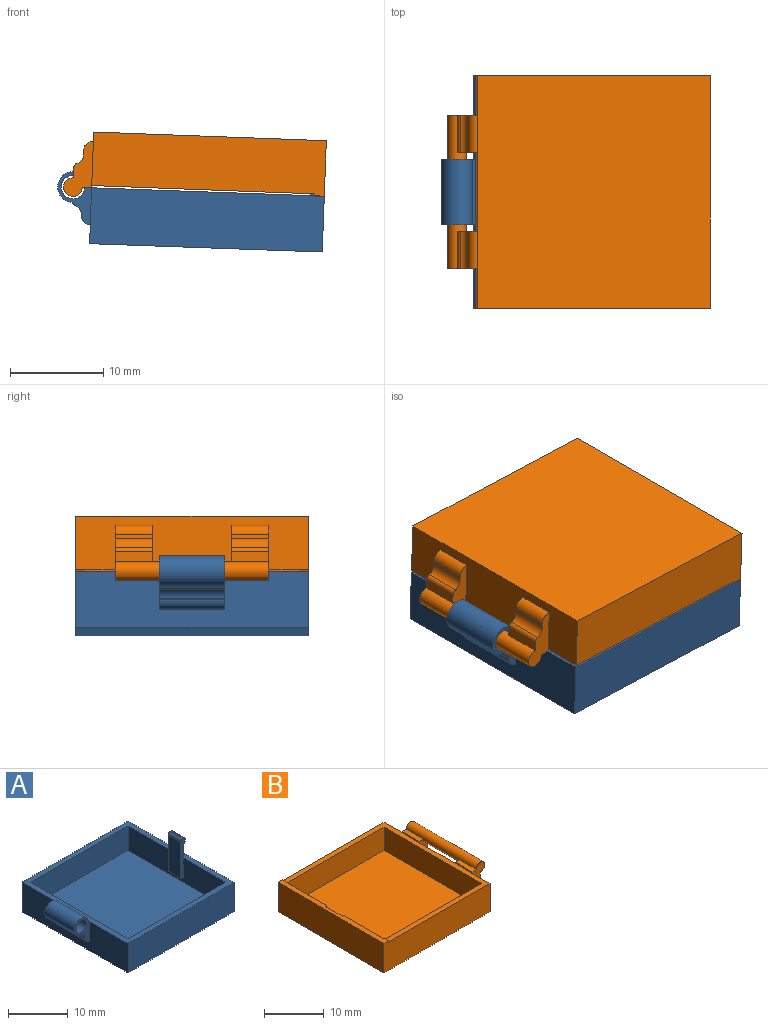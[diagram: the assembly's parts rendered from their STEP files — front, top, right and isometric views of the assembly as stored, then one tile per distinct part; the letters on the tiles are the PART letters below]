
ASSEMBLY  parts=2 mates=1
PART A: 30 faces, bbox 28.7x25x9.9 mm
  f0: plane 25x6mm, normal (-1,0,0), area 122mm2, adj f1,f2,f8,f9,f11,f12,f14
  f1: plane 25x6mm, normal (0,1,0), area 150mm2, adj f0,f7,f8,f9
  f2: plane 25x6mm, normal (0,-1,0), area 150mm2, adj f0,f7,f8,f9
  f3: plane 23x5mm, normal (0,-1,0), area 115mm2, adj f4,f6,f8,f10
  f4: plane 23x5mm, normal (-1,0,0), area 103mm2, adj f3,f5,f8,f10,f19,f20,f21
  f5: plane 23x5mm, normal (0,1,0), area 115mm2, adj f4,f6,f8,f10
  f6: plane 23x5mm, normal (1,0,0), area 115mm2, adj f3,f5,f8,f10
  f7: plane 25x6mm, normal (1,0,0), area 150mm2, adj f1,f2,f8,f9
  f8: plane 25.35x25mm, normal (0,0,1), area 98.4mm2, adj f0,f1,f2,f3,f4,f5,f6,f7
  f9: plane 25x25mm, normal (0,0,-1), area 625mm2, adj f0,f1,f2,f7
  f10: plane 23x23mm, normal (0,0,1), area 529mm2, adj f3,f4,f5,f6
  f11: plane 5.65x3.65mm, normal (0,1,0), area 7.4mm2, adj f0,f8,f13,f14,f15,f16,f17,f18
  f12: plane 5.65x3.65mm, normal (0,-1,0), area 7.4mm2, adj f0,f8,f13,f14,f15,f16,f17,f18
  f13: plane 7x0.09mm, normal (-1,0,0), area 0.6mm2, adj f11,f12,f14,f16
  f14: cylinder r=1mm len=7mm, axis (0,1,0), area 11mm2, adj f0,f11,f12,f13
  f15: cylinder r=0.5mm len=7mm, axis (0,1,0), area 3.2mm2, adj f11,f12,f16,f18
  f16: cylinder r=1mm len=7mm, axis (0,1,0), area 8.6mm2, adj f11,f12,f13,f15
  f17: cylinder r=1.25mm len=7mm, axis (0,-1,0), area 55mm2, adj f11,f12
  f18: cylinder r=1.65mm len=7mm, axis (0,-1,0), area 54.6mm2, adj f8,f11,f12,f15
  f19: plane 7.9x1mm, normal (0,1,0), area 4.4mm2, adj f4,f20,f22,f23,f24,f25,f26,f27
  f20: plane 3x0.5mm, normal (0,0,-1), area 1.5mm2, adj f4,f19,f21,f23
  f21: plane 7.9x1mm, normal (0,-1,0), area 4.4mm2, adj f4,f20,f22,f23,f24,f25,f26,f27
  f22: plane 3x0.25mm, normal (0,0,1), area 0.8mm2, adj f19,f21,f27,f29
  f23: plane 7.4x3mm, normal (-1,0,0), area 22.2mm2, adj f19,f20,f21,f29
  f24: plane 3x2.9mm, normal (1,0,0), area 8.7mm2, adj f8,f19,f21,f25
  f25: plane 3x0.25mm, normal (0,0,-1), area 0.8mm2, adj f19,f21,f24,f28
  f26: plane 3x0.5mm, normal (1,0,0), area 1.5mm2, adj f19,f21,f27,f28
  f27: cylinder r=0.25mm len=3mm, axis (0,1,0), area 1.2mm2, adj f19,f21,f22,f26
  f28: cylinder r=0.25mm len=3mm, axis (0,1,0), area 1.2mm2, adj f19,f21,f25,f26
  f29: cylinder r=0.5mm len=3mm, axis (0,-1,0), area 2.4mm2, adj f19,f21,f22,f23
PART B: 40 faces, bbox 28x25x7 mm
  f0: plane 4x1mm, normal (0,0,1), area 4mm2, adj f16,f17,f27,f35
  f1: plane 4x1mm, normal (0,0,1), area 4mm2, adj f13,f14,f27,f36
  f2: plane 25x6mm, normal (0,1,0), area 144mm2, adj f4,f8,f10,f11,f37,f39
  f3: plane 25x6mm, normal (0,-1,0), area 144mm2, adj f4,f8,f10,f11,f38,f39
  f4: plane 25x5.75mm, normal (1,0,0), area 105.8mm2, adj f2,f3,f11,f13,f14,f16,f17,f21
  f5: plane 23x4.75mm, normal (-1,0,0), area 109.2mm2, adj f6,f7,f12,f39
  f6: plane 23x5mm, normal (0,1,0), area 109.3mm2, adj f5,f8,f9,f12,f38,f39
  f7: plane 23x5mm, normal (0,-1,0), area 109.3mm2, adj f5,f8,f9,f12,f37,f39
  f8: plane 25x1.1mm, normal (0,0,1), area 23.8mm2, adj f2,f3,f6,f7,f9,f10,f31,f33
  f9: plane 23x5mm, normal (1,0,0), area 99mm2, adj f6,f7,f8,f12,f29,f30,f31,f33
  f10: plane 25x6mm, normal (-1,0,0), area 150mm2, adj f2,f3,f8,f11
  f11: plane 25x25mm, normal (0,0,-1), area 625mm2, adj f2,f3,f4,f10
  f12: plane 23x23mm, normal (0,0,1), area 529mm2, adj f5,f6,f7,f9
  f13: plane 6x3mm, normal (0,-1,0), area 9.8mm2, adj f1,f4,f15,f19,f22,f24,f26,f27
  f14: plane 5x2mm, normal (0,1,0), area 6.7mm2, adj f1,f4,f15,f19,f22,f24,f26,f27
  f15: plane 4x1.09mm, normal (1,0,0), area 4.3mm2, adj f13,f14,f26,f27
  f16: plane 5x2mm, normal (0,-1,0), area 6.7mm2, adj f0,f4,f18,f20,f21,f23,f25,f27
  f17: plane 6x3mm, normal (0,1,0), area 9.8mm2, adj f0,f4,f18,f20,f21,f23,f25,f27
  f18: plane 4x1.09mm, normal (1,0,0), area 4.3mm2, adj f16,f17,f25,f27
  f19: plane 4x0.5mm, normal (1,0,0), area 2mm2, adj f13,f14,f22,f24
  f20: plane 4x0.5mm, normal (1,0,0), area 2mm2, adj f16,f17,f21,f23
  f21: cylinder r=1mm len=4mm, axis (0,-1,0), area 6.3mm2, adj f4,f16,f17,f20
  f22: cylinder r=1mm len=4mm, axis (0,-1,0), area 6.3mm2, adj f4,f13,f14,f19
  f23: cylinder r=1mm len=4mm, axis (0,1,0), area 4.9mm2, adj f16,f17,f20,f25
  f24: cylinder r=1mm len=4mm, axis (0,1,0), area 4.9mm2, adj f13,f14,f19,f26
  f25: cylinder r=0.5mm len=4mm, axis (0,1,0), area 2.5mm2, adj f16,f17,f18,f23
  f26: cylinder r=0.5mm len=4mm, axis (0,1,0), area 2.5mm2, adj f13,f14,f15,f24
  f27: cylinder r=1mm len=16.5mm, axis (0,-1,0), area 91.2mm2, adj f0,f1,f13,f14,f15,f16,f17,f18
  f28: plane 4x0.25mm, normal (0,0,-1), area 1mm2, adj f29,f31,f32,f34
  f29: plane 0.9x0.6mm, normal (0,1,0), area 0.5mm2, adj f9,f28,f30,f32,f33
  f30: plane 4x0.6mm, normal (0,0,1), area 2.4mm2, adj f9,f29,f31,f32
  f31: plane 4x0.6mm, normal (0,-1,0), area 1.6mm2, adj f8,f9,f28,f30,f32,f34
  f32: plane 4x0.9mm, normal (1,0,0), area 3.6mm2, adj f28,f29,f30,f31
  f33: plane 3.1x0.35mm, normal (0,1,0), area 1.1mm2, adj f8,f9,f29,f34
  f34: plane 4x3.1mm, normal (1,0,0), area 12.4mm2, adj f8,f28,f31,f33
  f35: plane 4x0.25mm, normal (-1,0,0), area 1mm2, adj f0,f16,f17,f39
  f36: plane 4x0.25mm, normal (-1,0,0), area 1mm2, adj f1,f13,f14,f39
  f37: plane 1x0.25mm, normal (1,0,0), area 0.3mm2, adj f2,f7,f8,f39
  f38: plane 1x0.25mm, normal (1,0,0), area 0.3mm2, adj f3,f6,f8,f39
  f39: plane 25x23.9mm, normal (0,0,1), area 70.8mm2, adj f2,f3,f4,f5,f6,f7,f35,f36
PLACE A rot(axis=(0,1,0),2.1deg) t=(-4.31,-0.04,-5.44)mm
PLACE B rot(axis=(0,-1,0),177.9deg) t=(-3.87,-0.04,6.55)mm
MATE revolute B.f27 <-> A.f17  axis (0,-1,0) through (-4.1,-0.04,0.55)mm
